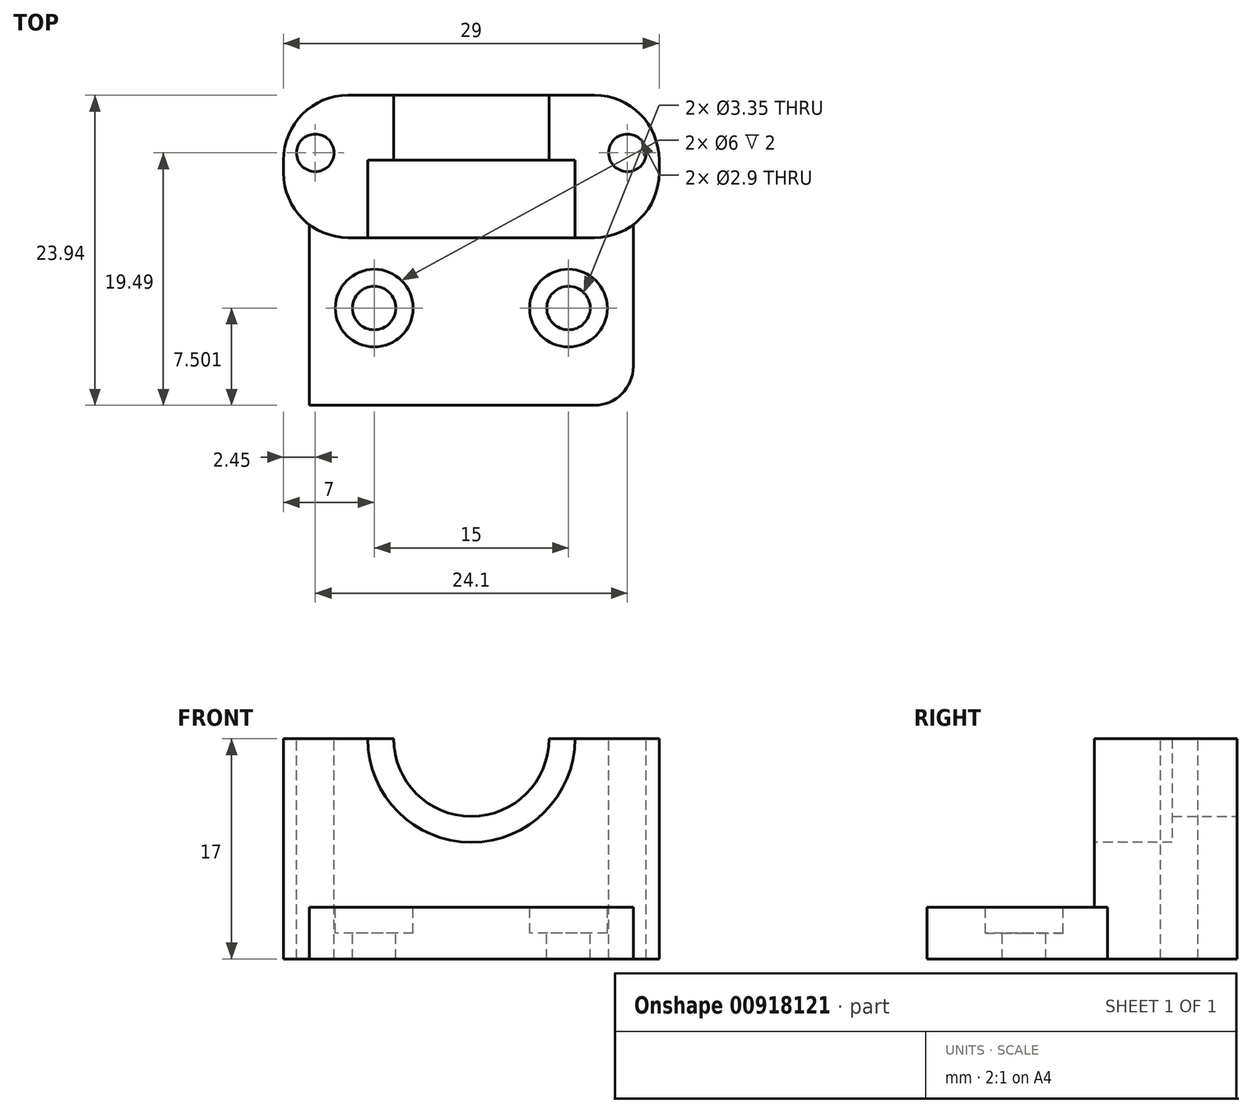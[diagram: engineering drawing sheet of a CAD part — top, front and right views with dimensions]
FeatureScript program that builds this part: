
annotation { "Feature Type Name" : "Feature", "Feature Type Description" : "" }
export const myFeature = defineFeature(function(context is Context, id is Id, definition is map)
    precondition{}
    {
        {
            var Q0;
            Q0=qCreatedBy(makeId("Top.planeOp"),FACE);
            var sketch = newSketch(context, id + "F0", { "sketchPlane" : qUnion([Q0])});
            skLineSegment(sketch, "E0.bottom", {"start": v(0, 0) * mm, "end": v(25, 0) * mm});
            skLineSegment(sketch, "E0.top", {"start": v(0, 35) * mm, "end": v(25, 35) * mm});
            skLineSegment(sketch, "E0.left", {"start": v(0, 0) * mm, "end": v(0, 35) * mm});
            skLineSegment(sketch, "E0.right", {"start": v(25, 0) * mm, "end": v(25, 35) * mm});
            skSolve(sketch);
        }
        {
            var Q0;
            Q0=qSketchRegion(id+"F0",true);
            extrude(context, id + "F1", {"entities" : qUnion([Q0]), "depth" : 4 * mm});
        }
        {
            var Q0;
            Q0=makeQuery(id+"F1.opExtrude","CAP_FACE",FACE,{"disambiguationData":[OSD([sQuery(id+"F0.wireOp",EDGE,"E0.bottom"),sQuery(id+"F0.wireOp",EDGE,"E0.top"),sQuery(id+"F0.wireOp",EDGE,"E0.left"),sQuery(id+"F0.wireOp",EDGE,"E0.right")])],"isStart":false});
            var sketch = newSketch(context, id + "F2", { "sketchPlane" : qUnion([Q0])});
            skCircle(sketch, "E1", {"center": v(5, 18.56) * mm, "radius": 1.68 * mm});
            skCircle(sketch, "E2", {"center": v(20, 18.56) * mm, "radius": 1.68 * mm});
            skCircle(sketch, "E3", {"center": v(5, 3.56) * mm, "radius": 1.68 * mm});
            skCircle(sketch, "E4", {"center": v(20, 3.56) * mm, "radius": 1.68 * mm});
            skLineSegment(sketch, "E5", {"start": v(5, 18.56) * mm, "end": v(0, 18.56) * mm});
            skLineSegment(sketch, "E6", {"start": v(20, 3.56) * mm, "end": v(25, 3.56) * mm});
            skCircle(sketch, "E7", {"center": v(5, 18.56) * mm, "radius": 3 * mm});
            skCircle(sketch, "E8", {"center": v(20, 18.56) * mm, "radius": 3 * mm});
            skCircle(sketch, "E9", {"center": v(5, 3.56) * mm, "radius": 3 * mm});
            skCircle(sketch, "E10", {"center": v(20, 3.56) * mm, "radius": 3 * mm});
            skSolve(sketch);
        }
        {
            var Q0;
            Q0=makeQuery(id+"F2.imprint","IMPRINT",FACE,{"disambiguationData":[TD([[makeQuery(id+"F2.imprint","IMPRINT",EDGE,{"derivedFrom":sQuery(id+"F2.wireOp",EDGE,"E1")}),1.0]])]});
            var Q1;
            Q1=makeQuery(id+"F2.imprint","IMPRINT",FACE,{"disambiguationData":[TD([[makeQuery(id+"F2.imprint","IMPRINT",EDGE,{"derivedFrom":sQuery(id+"F2.wireOp",EDGE,"E2")}),1.0]])]});
            var Q2;
            Q2=makeQuery(id+"F2.imprint","IMPRINT",FACE,{"disambiguationData":[TD([[makeQuery(id+"F2.imprint","IMPRINT",EDGE,{"derivedFrom":sQuery(id+"F2.wireOp",EDGE,"E4")}),1.0]])]});
            var Q3;
            Q3=makeQuery(id+"F2.imprint","IMPRINT",FACE,{"disambiguationData":[TD([[makeQuery(id+"F2.imprint","IMPRINT",EDGE,{"derivedFrom":sQuery(id+"F2.wireOp",EDGE,"E3")}),1.0]])]});
            extrude(context, id + "F3", {"entities" : qUnion([Q0, Q1, Q2, Q3]), "operationType" : NewBodyOperationType.REMOVE, "oppositeDirection" : true, "depth" : 25 * mm});
        }
        {
            var Q0;
            Q0=makeQuery(id+"F1.opExtrude","CAP_FACE",FACE,{"disambiguationData":[OSD([sQuery(id+"F0.wireOp",EDGE,"E0.bottom"),sQuery(id+"F0.wireOp",EDGE,"E0.top"),sQuery(id+"F0.wireOp",EDGE,"E0.left"),sQuery(id+"F0.wireOp",EDGE,"E0.right")])],"isStart":false});
            var sketch = newSketch(context, id + "F4", { "sketchPlane" : qUnion([Q0])});
            skLineSegment(sketch, "E11.bottom", {"start": v(0, 35) * mm, "end": v(25, 35) * mm});
            skLineSegment(sketch, "E11.top", {"start": v(0, 24) * mm, "end": v(25, 24) * mm});
            skLineSegment(sketch, "E11.left", {"start": v(0, 35) * mm, "end": v(0, 24) * mm});
            skLineSegment(sketch, "E11.right", {"start": v(25, 35) * mm, "end": v(25, 24) * mm});
            skSolve(sketch);
        }
        {
            var Q0;
            Q0=qSketchRegion(id+"F4",true);
            extrude(context, id + "F5", {"entities" : qUnion([Q0]), "operationType" : NewBodyOperationType.ADD, "depth" : 13 * mm});
        }
        {
            var Q0;
            Q0=makeQuery(id+"F5.boolean.opBoolean","MERGE",FACE,{"derivedFrom":[makeQuery(id+"F1.opExtrude","SWEPT_FACE",FACE,{"disambiguationData":[OSD([sQuery(id+"F0.wireOp",EDGE,"E0.top")])]}),makeQuery(id+"F5.opExtrude","SWEPT_FACE",FACE,{"disambiguationData":[OSD([sQuery(id+"F4.wireOp",EDGE,"E11.bottom")])]})]});
            var sketch = newSketch(context, id + "F6", { "sketchPlane" : qUnion([Q0])});
            skCircle(sketch, "E12", {"center": v(-12.5, 17) * mm, "radius": 6 * mm});
            skSolve(sketch);
        }
        {
            var Q0;
            {var subQ0=makeQuery(id+"F5.opExtrude","CAP_EDGE",EDGE,{"disambiguationData":[OSD([sQuery(id+"F4.wireOp",EDGE,"E11.bottom")])],"isStart":false});var subQ1=sQuery(id+"F6.wireOp",EDGE,"E12");var subQ3=makeQuery(id+"F6.imprint","INTERSECT",VERTEX,{"disambiguationData":[OD(0.0)],"derivedFrom":[subQ0,subQ1]});Q0=makeQuery(id+"F6.imprint","IMPRINT",FACE,{"disambiguationData":[TD([[makeQuery(id+"F6.imprint","IMPRINT",EDGE,{"disambiguationData":[TD([[subQ3,1.0]])],"derivedFrom":subQ1}),1.0]])]});}
            extrude(context, id + "F7", {"entities" : qUnion([Q0]), "operationType" : NewBodyOperationType.REMOVE, "oppositeDirection" : true, "depth" : 6 * mm});
        }
        {
            var Q0;
            Q0=makeQuery(id+"F5.opExtrude","SWEPT_FACE",FACE,{"disambiguationData":[OSD([sQuery(id+"F4.wireOp",EDGE,"E11.top")])]});
            var sketch = newSketch(context, id + "F8", { "sketchPlane" : qUnion([Q0])});
            skCircle(sketch, "E13", {"center": v(12.5, 17) * mm, "radius": 8 * mm});
            skSolve(sketch);
        }
        {
            var Q0;
            Q0=qSketchRegion(id+"F8",true);
            extrude(context, id + "F9", {"entities" : qUnion([Q0]), "operationType" : NewBodyOperationType.REMOVE, "oppositeDirection" : true, "depth" : 6 * mm});
        }
        {
            var Q0;
            Q0=makeQuery(id+"F2.imprint","IMPRINT",FACE,{"disambiguationData":[TD([[makeQuery(id+"F2.imprint","IMPRINT",EDGE,{"derivedFrom":sQuery(id+"F2.wireOp",EDGE,"E1")}),-1.0]])]});
            var Q1;
            Q1=makeQuery(id+"F2.imprint","IMPRINT",FACE,{"disambiguationData":[TD([[makeQuery(id+"F2.imprint","IMPRINT",EDGE,{"derivedFrom":sQuery(id+"F2.wireOp",EDGE,"E2")}),-1.0]])]});
            var Q2;
            Q2=makeQuery(id+"F2.imprint","IMPRINT",FACE,{"disambiguationData":[TD([[makeQuery(id+"F2.imprint","IMPRINT",EDGE,{"derivedFrom":sQuery(id+"F2.wireOp",EDGE,"E4")}),-1.0]])]});
            var Q3;
            Q3=makeQuery(id+"F2.imprint","IMPRINT",FACE,{"disambiguationData":[TD([[makeQuery(id+"F2.imprint","IMPRINT",EDGE,{"derivedFrom":sQuery(id+"F2.wireOp",EDGE,"E3")}),-1.0]])]});
            extrude(context, id + "F10", {"entities" : qUnion([Q0, Q1, Q2, Q3]), "operationType" : NewBodyOperationType.REMOVE, "oppositeDirection" : true, "depth" : 2 * mm});
        }
        {
            var Q0;
            Q0=makeQuery(id+"F1.opExtrude","SWEPT_EDGE",EDGE,{"disambiguationData":[OSD([sQuery(id+"F0.wireOp",EDGE,"E0.bottom"),sQuery(id+"F0.wireOp",EDGE,"E0.left")])]});
            var Q1;
            Q1=makeQuery(id+"F1.opExtrude","SWEPT_EDGE",EDGE,{"disambiguationData":[OSD([sQuery(id+"F0.wireOp",EDGE,"E0.bottom"),sQuery(id+"F0.wireOp",EDGE,"E0.right")])]});
            fillet(context, id + "F11", {"entities" : qUnion([Q0, Q1]), "radius" : 5 * mm, "tangentPropagation" : true, "allowEdgeOverflow" : false});
        }
        {
            var Q0;
            Q0=makeQuery(id+"F5.boolean.opBoolean","MERGE",FACE,{"derivedFrom":[makeQuery(id+"F1.opExtrude","SWEPT_FACE",FACE,{"disambiguationData":[OSD([sQuery(id+"F0.wireOp",EDGE,"E0.left")])]}),makeQuery(id+"F5.opExtrude","SWEPT_FACE",FACE,{"disambiguationData":[OSD([sQuery(id+"F4.wireOp",EDGE,"E11.left")])]})]});
            var sketch = newSketch(context, id + "F12", { "sketchPlane" : qUnion([Q0])});
            skLineSegment(sketch, "E14.bottom", {"start": v(-35, 0) * mm, "end": v(-24, 0) * mm});
            skLineSegment(sketch, "E14.top", {"start": v(-35, 17) * mm, "end": v(-24, 17) * mm});
            skLineSegment(sketch, "E14.left", {"start": v(-35, 0) * mm, "end": v(-35, 17) * mm});
            skLineSegment(sketch, "E14.right", {"start": v(-24, 0) * mm, "end": v(-24, 17) * mm});
            skSolve(sketch);
        }
        {
            var Q0;
            Q0=qSketchRegion(id+"F12",true);
            extrude(context, id + "F13", {"entities" : qUnion([Q0]), "operationType" : NewBodyOperationType.ADD, "depth" : 2 * mm});
        }
        {
            var Q0;
            Q0=makeQuery(id+"F5.boolean.opBoolean","MERGE",FACE,{"derivedFrom":[makeQuery(id+"F1.opExtrude","SWEPT_FACE",FACE,{"disambiguationData":[OSD([sQuery(id+"F0.wireOp",EDGE,"E0.right")])]}),makeQuery(id+"F5.opExtrude","SWEPT_FACE",FACE,{"disambiguationData":[OSD([sQuery(id+"F4.wireOp",EDGE,"E11.right")])]})]});
            var sketch = newSketch(context, id + "F14", { "sketchPlane" : qUnion([Q0])});
            skLineSegment(sketch, "E15.bottom", {"start": v(35, 0) * mm, "end": v(24, 0) * mm});
            skLineSegment(sketch, "E15.top", {"start": v(35, 17) * mm, "end": v(24, 17) * mm});
            skLineSegment(sketch, "E15.left", {"start": v(35, 0) * mm, "end": v(35, 17) * mm});
            skLineSegment(sketch, "E15.right", {"start": v(24, 0) * mm, "end": v(24, 17) * mm});
            skSolve(sketch);
        }
        {
            var Q0;
            Q0=qSketchRegion(id+"F14",true);
            extrude(context, id + "F15", {"entities" : qUnion([Q0]), "operationType" : NewBodyOperationType.ADD, "depth" : 2 * mm});
        }
        {
            var Q0;
            {var subQ0=sQuery(id+"F4.wireOp",EDGE,"E11.bottom");var subQ1=sQuery(id+"F4.wireOp",EDGE,"E11.top");var subQ2=sQuery(id+"F4.wireOp",EDGE,"E11.left");Q0=makeQuery(id+"F9.boolean.opBoolean","SPLIT",FACE,{"disambiguationData":[TD([makeQuery(id+"F1.opExtrude","SWEPT_FACE",FACE,{"disambiguationData":[OSD([sQuery(id+"F0.wireOp",EDGE,"E0.left")])]})])],"derivedFrom":makeQuery(id+"F5.opExtrude","CAP_FACE",FACE,{"disambiguationData":[OSD([subQ0,subQ1,subQ2,sQuery(id+"F4.wireOp",EDGE,"E11.right")])],"isStart":false})});}
            var sketch = newSketch(context, id + "F16", { "sketchPlane" : qUnion([Q0])});
            skCircle(sketch, "E16", {"center": v(0.45, 30.55) * mm, "radius": 1.45 * mm});
            skCircle(sketch, "E17", {"center": v(24.55, 30.55) * mm, "radius": 1.45 * mm});
            skSolve(sketch);
        }
        {
            var Q0;
            Q0=qSketchRegion(id+"F16",true);
            extrude(context, id + "F17", {"entities" : qUnion([Q0]), "operationType" : NewBodyOperationType.REMOVE, "oppositeDirection" : true, "depth" : 25 * mm});
        }
        {
            var Q0;
            Q0=makeQuery(id+"F13.opExtrude","CAP_EDGE",EDGE,{"disambiguationData":[OSD([sQuery(id+"F12.wireOp",EDGE,"E14.right")])],"isStart":false});
            var Q1;
            Q1=makeQuery(id+"F13.opExtrude","CAP_EDGE",EDGE,{"disambiguationData":[OSD([sQuery(id+"F12.wireOp",EDGE,"E14.left")])],"isStart":false});
            var Q2;
            Q2=makeQuery(id+"F15.opExtrude","CAP_EDGE",EDGE,{"disambiguationData":[OSD([sQuery(id+"F14.wireOp",EDGE,"E15.left")])],"isStart":false});
            var Q3;
            Q3=makeQuery(id+"F15.opExtrude","CAP_EDGE",EDGE,{"disambiguationData":[OSD([sQuery(id+"F14.wireOp",EDGE,"E15.right")])],"isStart":false});
            fillet(context, id + "F18", {"entities" : qUnion([Q0, Q1, Q2, Q3]), "radius" : 5 * mm, "tangentPropagation" : true, "allowEdgeOverflow" : false});
        }
        {
            var Q0;
            Q0=makeQuery(id+"F1.opExtrude","CAP_FACE",FACE,{"disambiguationData":[OSD([sQuery(id+"F0.wireOp",EDGE,"E0.bottom"),sQuery(id+"F0.wireOp",EDGE,"E0.top"),sQuery(id+"F0.wireOp",EDGE,"E0.left"),sQuery(id+"F0.wireOp",EDGE,"E0.right")])],"isStart":false});
            var sketch = newSketch(context, id + "F19", { "sketchPlane" : qUnion([Q0])});
            skLineSegment(sketch, "E18", {"start": v(5, 18.56) * mm, "end": v(5, 3.56) * mm});
            skLineSegment(sketch, "E19", {"start": v(0, 11.06) * mm, "end": v(25, 11.06) * mm});
            skPoint(sketch, "E19.startSnap0", {"position": v(5, 11.06) * mm});
            skLineSegment(sketch, "E20", {"start": v(0, 11.06) * mm, "end": v(0, 5) * mm});
            skLineSegment(sketch, "E21", {"start": v(25, 11.06) * mm, "end": v(25, 5) * mm});
            skLineSegment(sketch, "E22.bottom", {"start": v(0, 11.06) * mm, "end": v(29.45, 11.06) * mm});
            skLineSegment(sketch, "E22.top", {"start": v(0, -4.73) * mm, "end": v(29.45, -4.73) * mm});
            skLineSegment(sketch, "E22.left", {"start": v(0, 11.06) * mm, "end": v(0, -4.73) * mm});
            skLineSegment(sketch, "E22.right", {"start": v(29.45, 11.06) * mm, "end": v(29.45, -4.73) * mm});
            skSolve(sketch);
        }
        {
            var Q0;
            Q0=qSketchRegion(id+"F19",true);
            extrude(context, id + "F20", {"entities" : qUnion([Q0]), "operationType" : NewBodyOperationType.REMOVE, "oppositeDirection" : true, "depth" : 25 * mm});
        }
        {
            var Q0;
            Q0=makeQuery(id+"F20.boolean.opBoolean","COPY",EDGE,{"derivedFrom":makeQuery(id+"F20.opExtrude","SWEPT_EDGE",EDGE,{"disambiguationData":[OSD([sQuery(id+"F0.wireOp",EDGE,"E0.left"),sQuery(id+"F19.wireOp",EDGE,"E22.bottom"),sQuery(id+"F19.wireOp",EDGE,"E22.left")])]})});
            var Q1;
            Q1=makeQuery(id+"F20.boolean.opBoolean","INTERSECT",EDGE,{"derivedFrom":[makeQuery(id+"F5.boolean.opBoolean","MERGE",FACE,{"derivedFrom":[makeQuery(id+"F1.opExtrude","SWEPT_FACE",FACE,{"disambiguationData":[OSD([sQuery(id+"F0.wireOp",EDGE,"E0.right")])]}),makeQuery(id+"F5.opExtrude","SWEPT_FACE",FACE,{"disambiguationData":[OSD([sQuery(id+"F4.wireOp",EDGE,"E11.right")])]})]}),makeQuery(id+"F20.opExtrude","SWEPT_FACE",FACE,{"disambiguationData":[OSD([sQuery(id+"F19.wireOp",EDGE,"E22.bottom")])]})]});
            fillet(context, id + "F21", {"entities" : qUnion([Q0, Q1]), "radius" : 3 * mm, "tangentPropagation" : true, "allowEdgeOverflow" : false});
        }
    });
